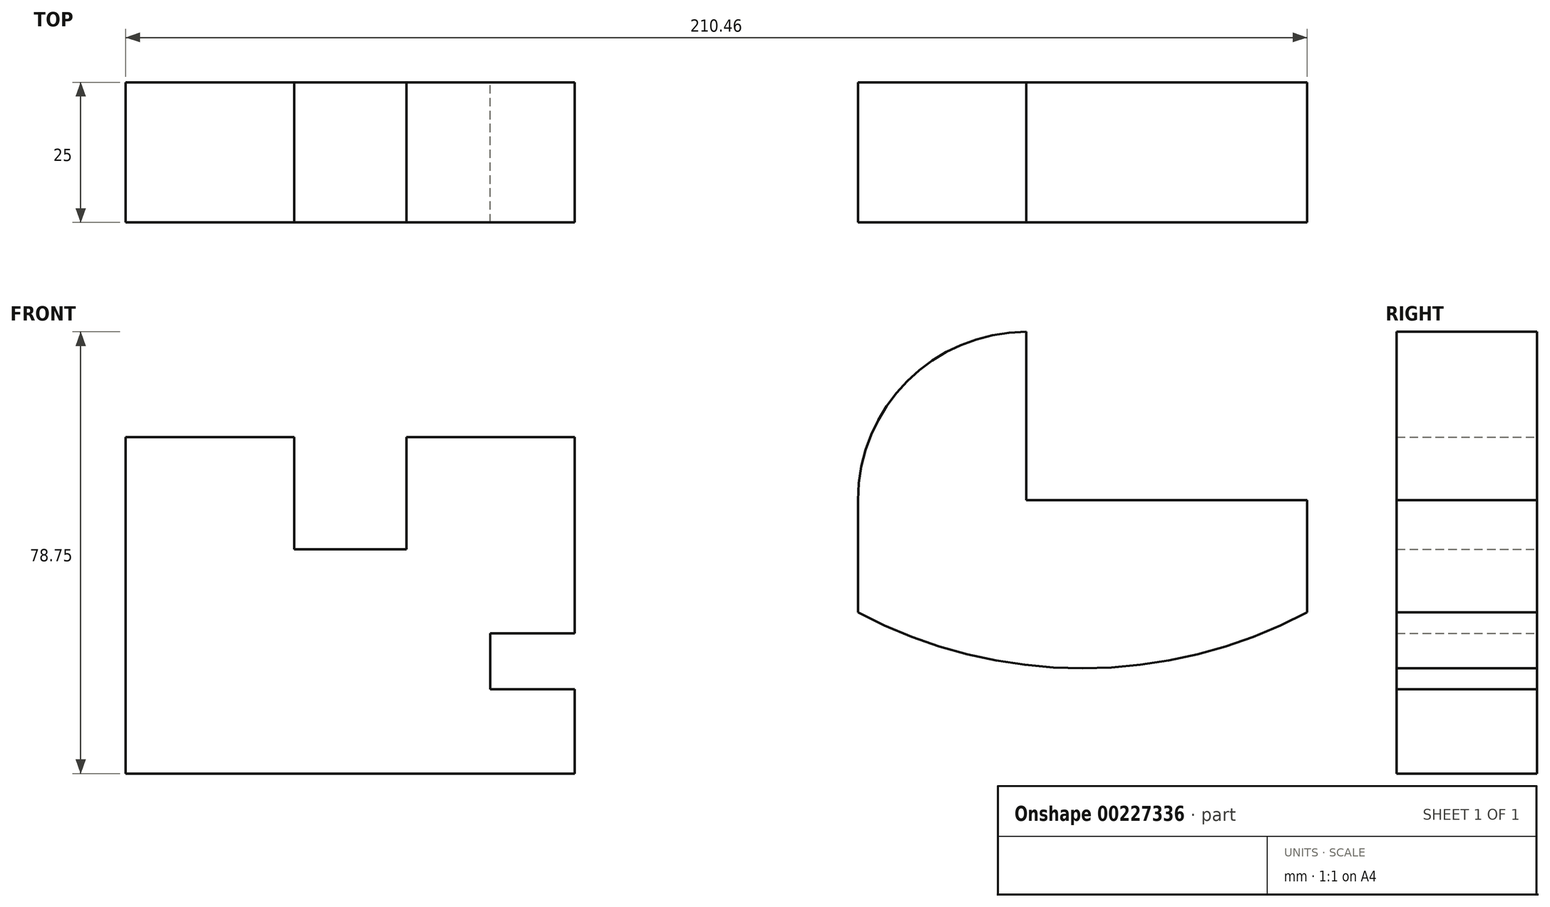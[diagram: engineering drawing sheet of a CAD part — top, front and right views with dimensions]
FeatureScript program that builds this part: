
annotation { "Feature Type Name" : "Feature", "Feature Type Description" : "" }
export const myFeature = defineFeature(function(context is Context, id is Id, definition is map)
    precondition{}
    {
        {
            var Q0;
            Q0=qCreatedBy(makeId("Front.planeOp"),FACE);
            var sketch = newSketch(context, id + "F0", { "sketchPlane" : qUnion([Q0])});
            skLineSegment(sketch, "E0", {"start": v(-67.04, 44.34) * mm, "end": v(-37.04, 44.34) * mm});
            skLineSegment(sketch, "E1", {"start": v(-37.04, 24.34) * mm, "end": v(-17.04, 24.34) * mm});
            skLineSegment(sketch, "E2", {"start": v(-17.04, 24.34) * mm, "end": v(-17.04, 44.34) * mm});
            skLineSegment(sketch, "E3", {"start": v(-17.04, 44.34) * mm, "end": v(12.96, 44.34) * mm});
            skLineSegment(sketch, "E4", {"start": v(-2.13, 9.34) * mm, "end": v(-2.13, -0.66) * mm});
            skLineSegment(sketch, "E5", {"start": v(-2.13, -0.66) * mm, "end": v(-2.13, 9.34) * mm});
            skLineSegment(sketch, "E6", {"start": v(12.96, 9.34) * mm, "end": v(-2.13, 9.34) * mm});
            skLineSegment(sketch, "E7", {"start": v(-2.13, -0.66) * mm, "end": v(12.96, -0.66) * mm});
            skLineSegment(sketch, "E8", {"start": v(12.96, -0.66) * mm, "end": v(12.96, -15.66) * mm});
            skLineSegment(sketch, "E9", {"start": v(-67.04, -15.66) * mm, "end": v(12.96, -15.66) * mm});
            skLineSegment(sketch, "E10", {"start": v(-67.04, 44.34) * mm, "end": v(-67.04, -15.66) * mm});
            skLineSegment(sketch, "E11", {"start": v(-37.04, 44.34) * mm, "end": v(-37.04, 24.34) * mm});
            skLineSegment(sketch, "E12", {"start": v(12.96, 9.34) * mm, "end": v(12.96, 44.34) * mm});
            skLineSegment(sketch, "E13", {"start": v(93.42, 63.1) * mm, "end": v(93.42, 33.1) * mm});
            skLineSegment(sketch, "E14", {"start": v(93.42, 33.1) * mm, "end": v(143.42, 33.1) * mm});
            skLineSegment(sketch, "E15", {"start": v(143.42, 33.1) * mm, "end": v(143.42, 13.1) * mm});
            skArc(sketch, "E16", {"start": v(63.42, 13.1) * mm, "mid": v(103.42, 3.1) * mm, "end": v(143.42, 13.1) * mm});
            skLineSegment(sketch, "E17", {"start": v(63.42, 13.1) * mm, "end": v(63.42, 33.1) * mm});
            skArc(sketch, "E18", {"start": v(93.42, 63.1) * mm, "mid": v(72.2, 54.3) * mm, "end": v(63.42, 33.1) * mm});
            skSolve(sketch);
        }
        {
            var Q0;
            Q0 = qSketchRegion(id + "F0", true);
            extrude(context, id + "F1", {"entities" : qUnion([Q0]), "depth" : 25 * mm});
        }
    });
